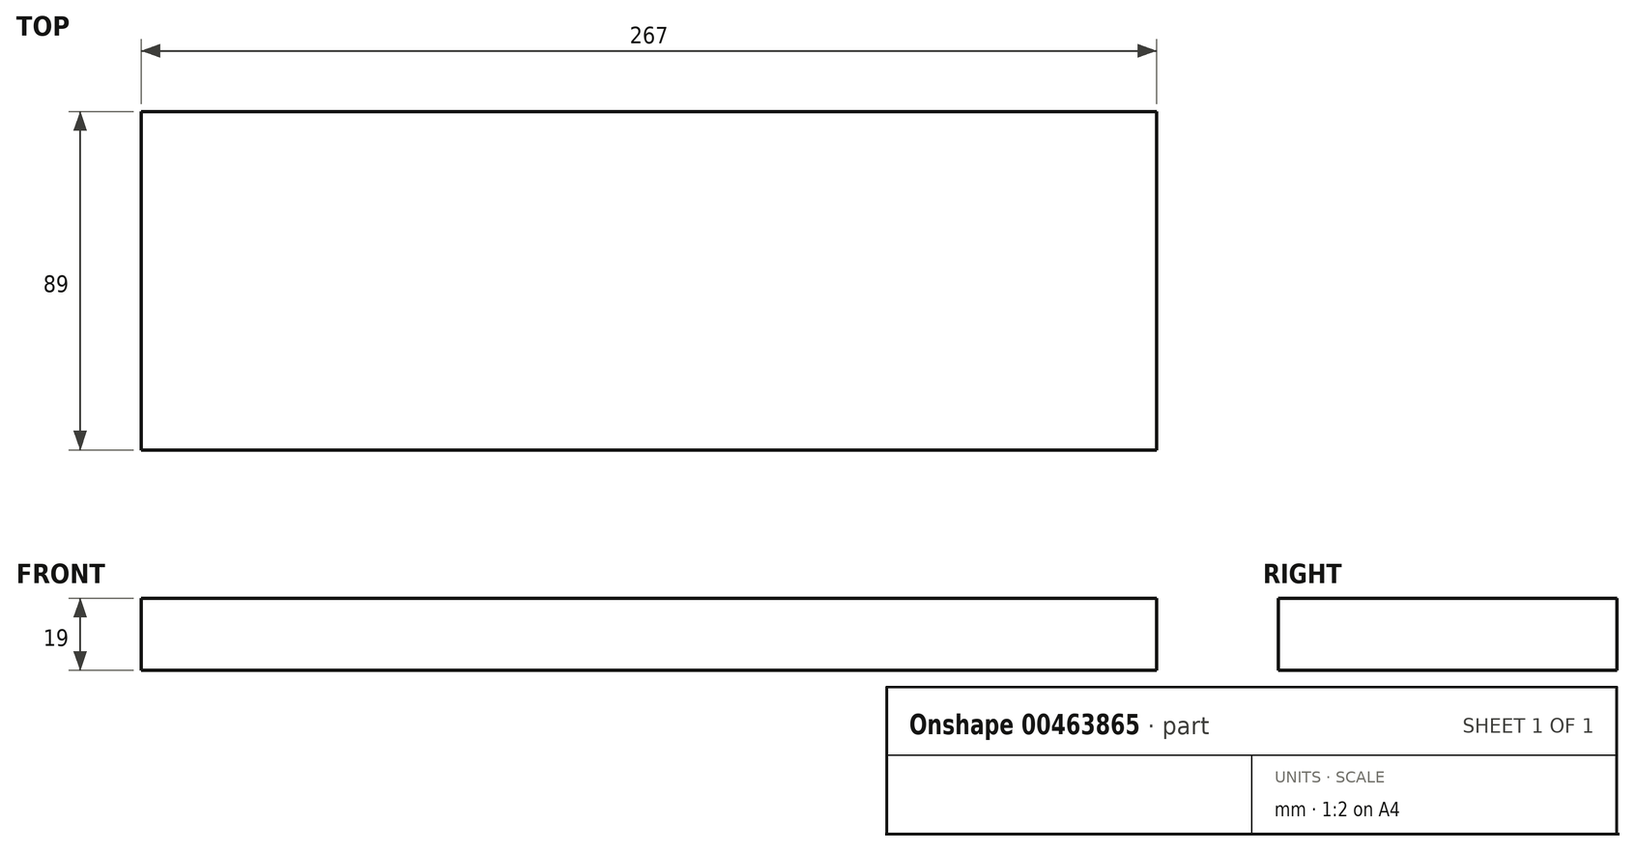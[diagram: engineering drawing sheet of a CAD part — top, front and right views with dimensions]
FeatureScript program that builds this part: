
annotation { "Feature Type Name" : "Feature", "Feature Type Description" : "" }
export const myFeature = defineFeature(function(context is Context, id is Id, definition is map)
    precondition{}
    {
        {
            var Q0;
            Q0=qCreatedBy(makeId("Top.planeOp"),FACE);
            var sketch = newSketch(context, id + "F0", { "sketchPlane" : qUnion([Q0])});
            skLineSegment(sketch, "E0.bottom", {"start": v(0, 89) * mm, "end": v(267, 89) * mm});
            skLineSegment(sketch, "E0.top", {"start": v(0, 0) * mm, "end": v(267, 0) * mm});
            skLineSegment(sketch, "E0.left", {"start": v(0, 89) * mm, "end": v(0, 0) * mm});
            skLineSegment(sketch, "E0.right", {"start": v(267, 89) * mm, "end": v(267, 0) * mm});
            skSolve(sketch);
        }
        {
            var Q0;
            Q0 = qSketchRegion(id + "F0", true);
            extrude(context, id + "F1", {"entities" : qUnion([Q0]), "depth" : 19 * mm});
        }
    });
